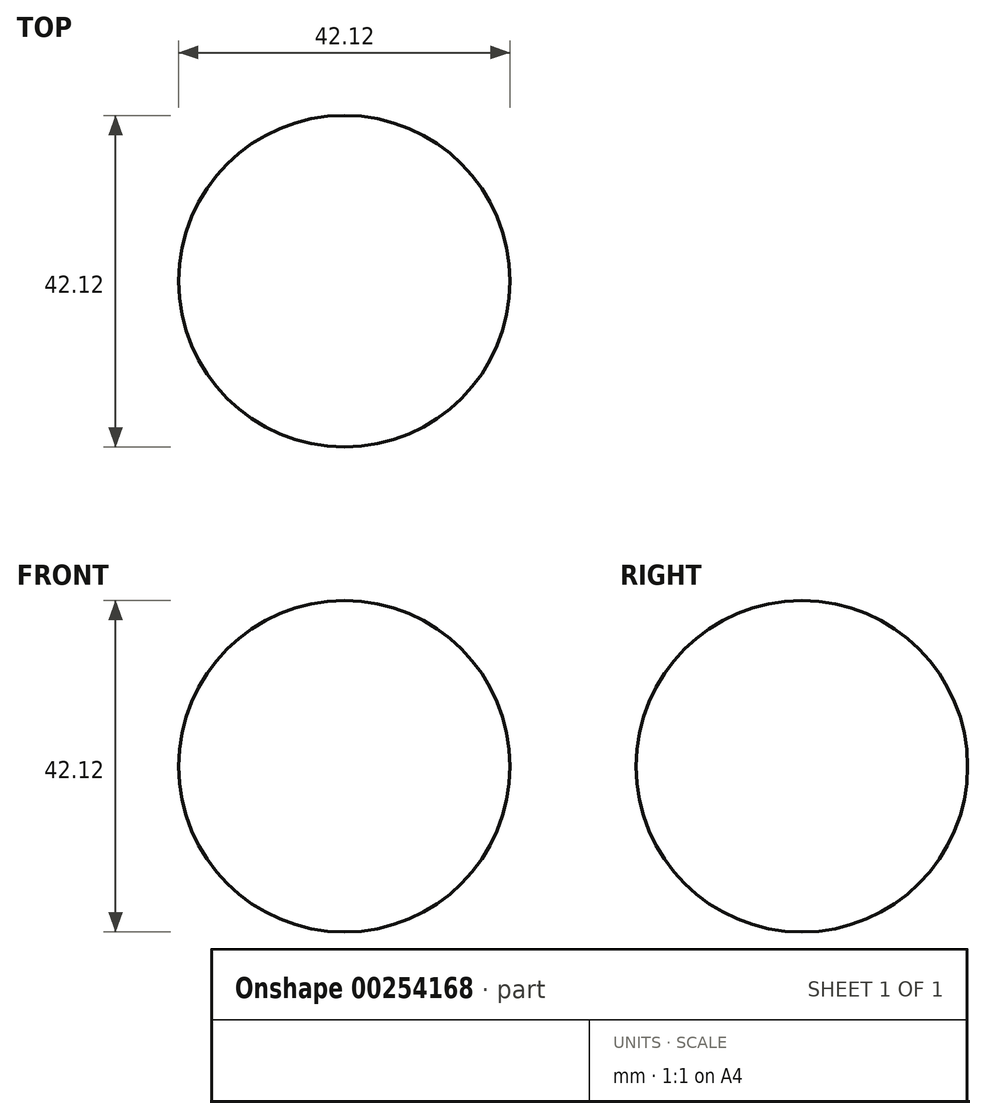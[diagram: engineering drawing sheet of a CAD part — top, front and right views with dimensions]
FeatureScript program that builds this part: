
annotation { "Feature Type Name" : "Feature", "Feature Type Description" : "" }
export const myFeature = defineFeature(function(context is Context, id is Id, definition is map)
    precondition{}
    {
        {
            var Q0;
            Q0=qCreatedBy(makeId("Front.planeOp"),FACE);
            var sketch = newSketch(context, id + "F0", { "sketchPlane" : qUnion([Q0])});
            skArc(sketch, "E0", {"start": v(0, -21.06) * mm, "mid": v(-21.06, 0) * mm, "end": v(0, 21.06) * mm});
            skLineSegment(sketch, "E1", {"start": v(0, 75.5) * mm, "end": v(0, -74.9) * mm, "construction": true});
            skSolve(sketch);
        }
        {
            var Q0;
            Q0=sQuery(id+"F0.wireOp",EDGE,"E0");
            var Q1;
            Q1=sQuery(id+"F0.wireOp",EDGE,"E1");
            revolve(context, id + "F1", {"bodyType" : ToolBodyType.SURFACE, "surfaceEntities" : qUnion([Q0]), "axis" : qUnion([Q1]), "revolveType" : RevolveType.FULL});
        }
    });
